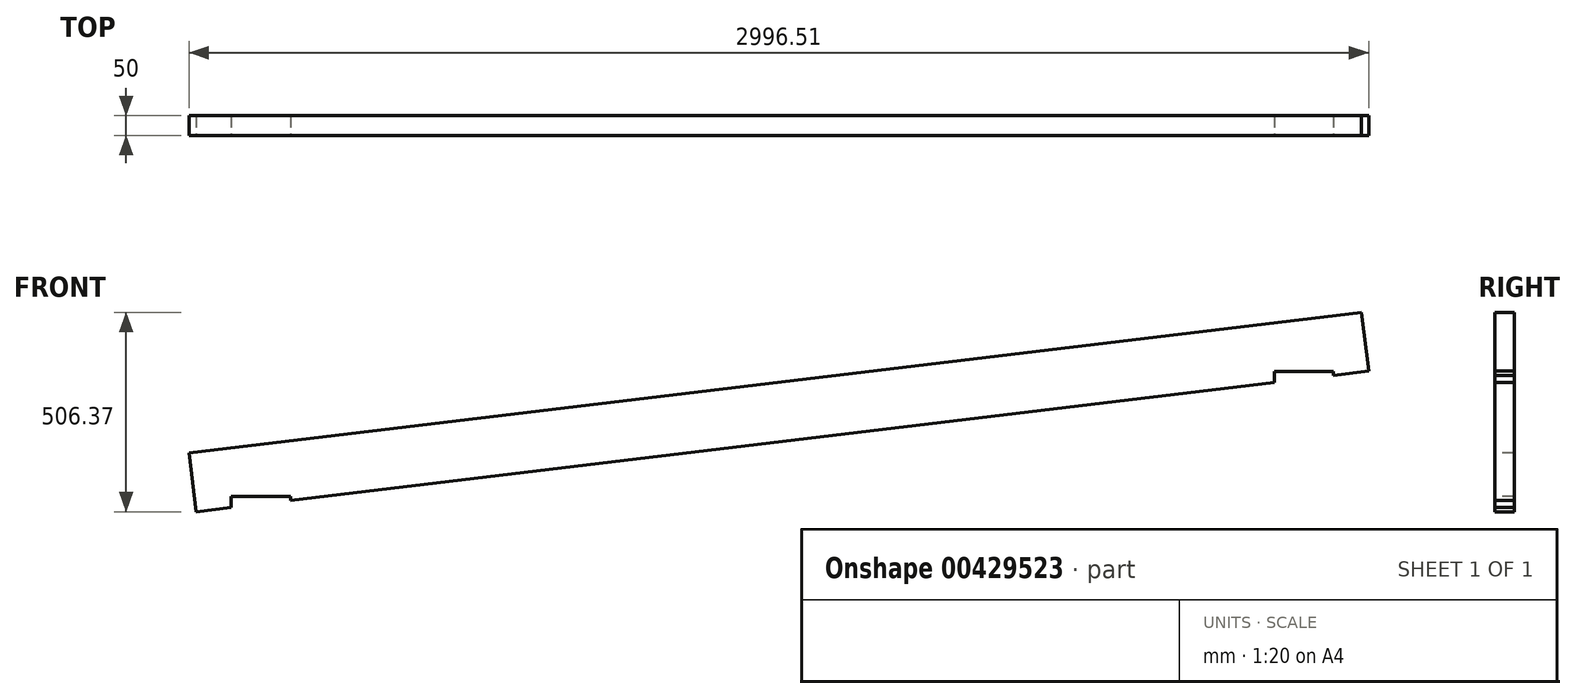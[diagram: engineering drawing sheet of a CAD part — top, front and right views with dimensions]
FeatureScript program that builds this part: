
annotation { "Feature Type Name" : "Feature", "Feature Type Description" : "" }
export const myFeature = defineFeature(function(context is Context, id is Id, definition is map)
    precondition{}
    {
        {
            var Q0;
            Q0=qCreatedBy(makeId("Front.planeOp"),FACE);
            var sketch = newSketch(context, id + "F0", { "sketchPlane" : qUnion([Q0])});
            skLineSegment(sketch, "E0.top", {"start": v(-2500, 0) * mm, "end": v(0, 0) * mm});
            skLineSegment(sketch, "E0.right", {"start": v(0, 300) * mm, "end": v(0, 0) * mm});
            skLineSegment(sketch, "E1", {"start": v(239.32, 328.72) * mm, "end": v(-2739.32, -28.72) * mm});
            skLineSegment(sketch, "E2", {"start": v(239.32, 328.72) * mm, "end": v(221.44, 477.65) * mm});
            skLineSegment(sketch, "E3", {"start": v(221.44, 477.65) * mm, "end": v(-2757.19, 120.21) * mm});
            skLineSegment(sketch, "E4", {"start": v(-2757.19, 120.21) * mm, "end": v(-2739.32, -28.72) * mm});
            skPoint(sketch, "E5", {"position": v(-1250, 150) * mm});
            skLineSegment(sketch, "E6", {"start": v(0, 300) * mm, "end": v(0, 328) * mm});
            skLineSegment(sketch, "E7", {"start": v(0, 328) * mm, "end": v(150, 328) * mm});
            skLineSegment(sketch, "E8", {"start": v(150, 328) * mm, "end": v(150, 318) * mm});
            skLineSegment(sketch, "E9", {"start": v(-2500, 0) * mm, "end": v(-2500, 10) * mm});
            skLineSegment(sketch, "E10", {"start": v(-2500, 10) * mm, "end": v(-2650, 10) * mm});
            skLineSegment(sketch, "E11", {"start": v(-2650, 10) * mm, "end": v(-2650, -18) * mm});
            skSolve(sketch);
        }
        {
            var Q0;
            {var subQ4=sQuery(id+"F0.wireOp",EDGE,"E2");Q0=makeQuery(id+"F0.imprint","IMPRINT",FACE,{"disambiguationData":[TD([[makeQuery(id+"F0.imprint","IMPRINT",EDGE,{"derivedFrom":subQ4}),1.0]])]});}
            extrude(context, id + "F1", {"entities" : qUnion([Q0]), "oppositeDirection" : true, "depth" : 50 * mm});
        }
    });
